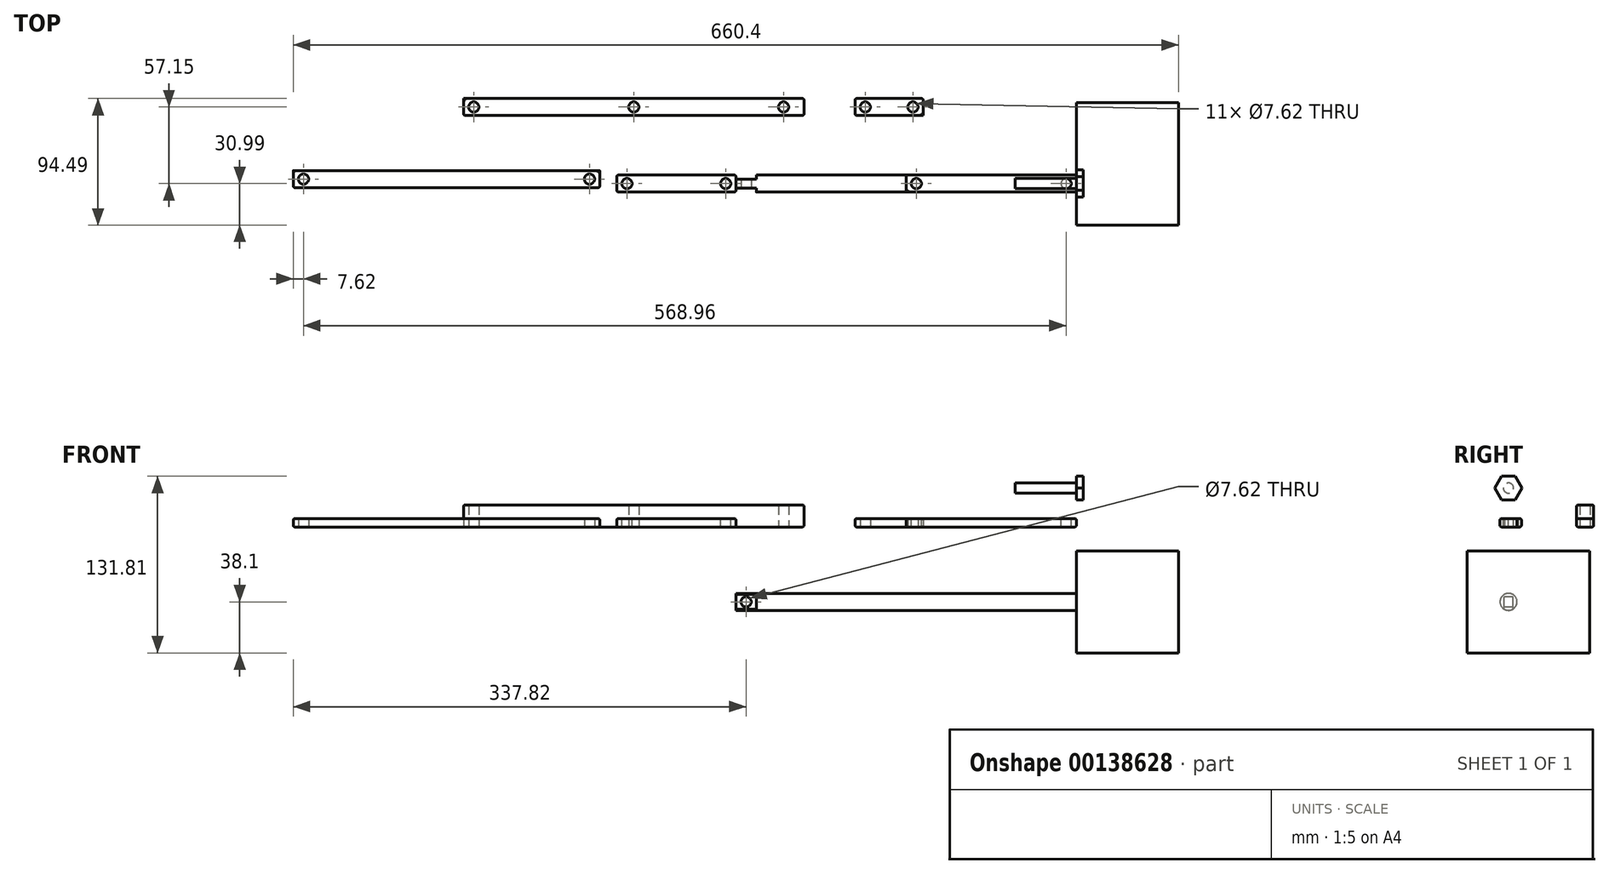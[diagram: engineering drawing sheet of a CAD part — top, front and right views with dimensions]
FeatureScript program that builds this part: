
annotation { "Feature Type Name" : "Feature", "Feature Type Description" : "" }
export const myFeature = defineFeature(function(context is Context, id is Id, definition is map)
    precondition{}
    {
        {
            var Q0;
            Q0=qCreatedBy(makeId("Right.planeOp"),FACE);
            var sketch = newSketch(context, id + "F0", { "sketchPlane" : qUnion([Q0])});
            skCircle(sketch, "E0", {"center": v(0, 0) * mm, "radius": 30.99 * mm});
            skSolve(sketch);
        }
        {
            var Q0;
            Q0 = qSketchRegion(id + "F0", true);
            extrude(context, id + "F1", {"entities" : qUnion([Q0]), "depth" : 76.2 * mm});
        }
        {
            var Q0;
            Q0=makeQuery(id+"F1.opExtrude","CAP_FACE",FACE,{"disambiguationData":[OSD([sQuery(id+"F0.wireOp",EDGE,"E0")])],"isStart":true});
            var sketch = newSketch(context, id + "F2", { "sketchPlane" : qUnion([Q0])});
            skCircle(sketch, "E1", {"center": v(0, 0) * mm, "radius": 6.35 * mm});
            skSolve(sketch);
        }
        {
            var Q0;
            Q0 = qSketchRegion(id + "F2", true);
            extrude(context, id + "F3", {"entities" : qUnion([Q0]), "operationType" : NewBodyOperationType.ADD, "depth" : 254 * mm});
        }
        {
            var Q0;
            Q0=qCreatedBy(makeId("Front.planeOp"),FACE);
            var sketch = newSketch(context, id + "F4", { "sketchPlane" : qUnion([Q0])});
            skCircle(sketch, "E2", {"center": v(-246.38, 0) * mm, "radius": 3.8 * mm});
            skSolve(sketch);
        }
        {
            var Q0;
            Q0 = qSketchRegion(id + "F4", true);
            extrude(context, id + "F5", {"entities" : qUnion([Q0]), "operationType" : NewBodyOperationType.REMOVE, "endBound" : BoundingType.SYMMETRIC, "oppositeDirection" : true, "depth" : 25.4 * mm});
        }
        {
            var Q0;
            Q0=qCreatedBy(makeId("Top.planeOp"),FACE);
            var sketch = newSketch(context, id + "F6", { "sketchPlane" : qUnion([Q0])});
            skLineSegment(sketch, "E3.bottom", {"start": v(-254, -6.35) * mm, "end": v(-238.76, -6.35) * mm});
            skLineSegment(sketch, "E3.top", {"start": v(-254, -3.3) * mm, "end": v(-238.76, -3.3) * mm});
            skLineSegment(sketch, "E3.left", {"start": v(-254, -6.35) * mm, "end": v(-254, -3.3) * mm});
            skLineSegment(sketch, "E3.right", {"start": v(-238.76, -6.35) * mm, "end": v(-238.76, -3.3) * mm});
            skLineSegment(sketch, "E4.bottom", {"start": v(-254, 6.35) * mm, "end": v(-238.76, 6.35) * mm});
            skLineSegment(sketch, "E4.top", {"start": v(-254, 3.3) * mm, "end": v(-238.76, 3.3) * mm});
            skLineSegment(sketch, "E4.left", {"start": v(-254, 6.35) * mm, "end": v(-254, 3.3) * mm});
            skLineSegment(sketch, "E4.right", {"start": v(-238.76, 6.35) * mm, "end": v(-238.76, 3.3) * mm});
            skSolve(sketch);
        }
        {
            var Q0;
            Q0 = qSketchRegion(id + "F6", true);
            extrude(context, id + "F7", {"entities" : qUnion([Q0]), "operationType" : NewBodyOperationType.REMOVE, "endBound" : BoundingType.SYMMETRIC, "oppositeDirection" : true, "depth" : 25.4 * mm});
        }
        {
            var Q0;
            Q0=qCreatedBy(makeId("Front.planeOp"),FACE);
            var sketch = newSketch(context, id + "F8", { "sketchPlane" : qUnion([Q0])});
            skLineSegment(sketch, "E5.bottom", {"start": v(0, 55.88) * mm, "end": v(-127, 55.88) * mm});
            skLineSegment(sketch, "E5.top", {"start": v(0, 62.23) * mm, "end": v(-127, 62.23) * mm});
            skLineSegment(sketch, "E5.left", {"start": v(0, 55.88) * mm, "end": v(0, 62.23) * mm});
            skLineSegment(sketch, "E5.right", {"start": v(-127, 55.88) * mm, "end": v(-127, 62.23) * mm});
            skSolve(sketch);
        }
        {
            var Q0;
            Q0=qCreatedBy(makeId("Top.planeOp"),FACE);
            cPlane(context, id + "F9", {"entities" : qUnion([Q0]), "cplaneType" : CPlaneType.OFFSET, "offset" : 55.88 * mm, "width" : 152.4 * mm, "height" : 152.4 * mm});
        }
        {
            var Q0;
            Q0=qCreatedBy(makeId("Top.planeOp"),FACE);
            var sketch = newSketch(context, id + "F10", { "sketchPlane" : qUnion([Q0])});
            skLineSegment(sketch, "E6.bottom", {"start": v(-238.76, 3.3) * mm, "end": v(-137.16, 3.3) * mm});
            skLineSegment(sketch, "E6.top", {"start": v(-238.76, 6.35) * mm, "end": v(-137.16, 6.35) * mm});
            skLineSegment(sketch, "E6.left", {"start": v(-238.76, 3.3) * mm, "end": v(-238.76, 6.35) * mm});
            skLineSegment(sketch, "E6.right", {"start": v(-137.16, 3.3) * mm, "end": v(-137.16, 6.35) * mm});
            skSolve(sketch);
        }
        {
            var Q0;
            Q0=qCreatedBy(makeId("Right.planeOp"),FACE);
            var sketch = newSketch(context, id + "F11", { "sketchPlane" : qUnion([Q0])});
            skCircle(sketch, "E7.cCircle", {"center": v(0, 84.9) * mm, "radius": 8.8 * mm, "construction": true});
            skLineSegment(sketch, "E7.0", {"start": v(5.08, 76.11) * mm, "end": v(-5.08, 76.11) * mm});
            skLineSegment(sketch, "E7.1", {"start": v(-5.08, 76.11) * mm, "end": v(-10.16, 84.9) * mm});
            skLineSegment(sketch, "E7.2", {"start": v(-10.16, 84.9) * mm, "end": v(-5.08, 93.7) * mm});
            skLineSegment(sketch, "E7.3", {"start": v(-5.08, 93.7) * mm, "end": v(5.08, 93.7) * mm});
            skLineSegment(sketch, "E7.4", {"start": v(5.08, 93.7) * mm, "end": v(10.16, 84.9) * mm});
            skLineSegment(sketch, "E7.5", {"start": v(10.16, 84.9) * mm, "end": v(5.08, 76.11) * mm});
            skPoint(sketch, "E7.0.midPoint", {"position": v(0, 76.11) * mm});
            skSolve(sketch);
        }
        {
            var Q0;
            Q0 = qSketchRegion(id + "F11", true);
            extrude(context, id + "F12", {"entities" : qUnion([Q0]), "depth" : 5.08 * mm});
        }
        {
            var Q0;
            Q0=makeQuery(id+"F12.opExtrude","CAP_FACE",FACE,{"disambiguationData":[OSD([sQuery(id+"F11.wireOp",EDGE,"E7.0"),sQuery(id+"F11.wireOp",EDGE,"E7.1"),sQuery(id+"F11.wireOp",EDGE,"E7.2"),sQuery(id+"F11.wireOp",EDGE,"E7.3"),sQuery(id+"F11.wireOp",EDGE,"E7.4"),sQuery(id+"F11.wireOp",EDGE,"E7.5")])],"isStart":false});
            var sketch = newSketch(context, id + "F13", { "sketchPlane" : qUnion([Q0])});
            skCircle(sketch, "E8", {"center": v(0, 84.9) * mm, "radius": 3.81 * mm});
            skSolve(sketch);
        }
        {
            var Q0;
            Q0 = qSketchRegion(id + "F13", true);
            extrude(context, id + "F14", {"entities" : qUnion([Q0]), "operationType" : NewBodyOperationType.ADD, "oppositeDirection" : true, "depth" : 50.8 * mm});
        }
        {
            var Q0;
            Q0=makeQuery(id+"F8.imprint","IMPRINT",FACE,{"disambiguationData":[TD([[makeQuery(id+"F8.imprint","IMPRINT",EDGE,{"derivedFrom":sQuery(id+"F8.wireOp",EDGE,"E5.bottom")}),-1.0]])]});
            extrude(context, id + "F15", {"entities" : qUnion([Q0]), "endBound" : BoundingType.SYMMETRIC, "depth" : 12.7 * mm});
        }
        {
            var Q0;
            Q0=makeQuery(id+"F15.opExtrude","SWEPT_FACE",FACE,{"disambiguationData":[OSD([sQuery(id+"F8.wireOp",EDGE,"E5.top")])]});
            var sketch = newSketch(context, id + "F16", { "sketchPlane" : qUnion([Q0])});
            skCircle(sketch, "E9", {"center": v(-7.62, 0) * mm, "radius": 3.81 * mm});
            skCircle(sketch, "E10", {"center": v(-119.38, 0) * mm, "radius": 3.81 * mm});
            skSolve(sketch);
        }
        {
            var Q0;
            Q0=makeQuery(id+"F16.imprint","IMPRINT",FACE,{"disambiguationData":[TD([[makeQuery(id+"F16.imprint","IMPRINT",EDGE,{"derivedFrom":sQuery(id+"F16.wireOp",EDGE,"E10")}),1.0]])]});
            var Q1;
            Q1=makeQuery(id+"F16.imprint","IMPRINT",FACE,{"disambiguationData":[TD([[makeQuery(id+"F16.imprint","IMPRINT",EDGE,{"derivedFrom":sQuery(id+"F16.wireOp",EDGE,"E9")}),1.0]])]});
            extrude(context, id + "F17", {"entities" : qUnion([Q0, Q1]), "operationType" : NewBodyOperationType.REMOVE, "oppositeDirection" : true, "depth" : 12.7 * mm});
        }
        {
            var Q0;
            Q0=qCreatedBy(id+"F9.planeOp",FACE);
            var sketch = newSketch(context, id + "F18", { "sketchPlane" : qUnion([Q0])});
            skLineSegment(sketch, "E11.bottom", {"start": v(-254, 6.35) * mm, "end": v(-342.9, 6.35) * mm});
            skLineSegment(sketch, "E11.top", {"start": v(-254, -6.35) * mm, "end": v(-342.9, -6.35) * mm});
            skLineSegment(sketch, "E11.left", {"start": v(-254, 6.35) * mm, "end": v(-254, -6.35) * mm});
            skLineSegment(sketch, "E11.right", {"start": v(-342.9, 6.35) * mm, "end": v(-342.9, -6.35) * mm});
            skSolve(sketch);
        }
        {
            var Q0;
            Q0 = qSketchRegion(id + "F18", true);
            extrude(context, id + "F19", {"entities" : qUnion([Q0]), "depth" : 6.35 * mm});
        }
        {
            var Q0;
            Q0=makeQuery(id+"F19.opExtrude","CAP_FACE",FACE,{"disambiguationData":[OSD([sQuery(id+"F18.wireOp",EDGE,"E11.bottom"),sQuery(id+"F18.wireOp",EDGE,"E11.top"),sQuery(id+"F18.wireOp",EDGE,"E11.left"),sQuery(id+"F18.wireOp",EDGE,"E11.right")])],"isStart":false});
            var sketch = newSketch(context, id + "F20", { "sketchPlane" : qUnion([Q0])});
            skCircle(sketch, "E12", {"center": v(-261.62, 0) * mm, "radius": 3.81 * mm});
            skPoint(sketch, "E12.centerSnap0", {"position": v(-254, 0) * mm});
            skCircle(sketch, "E13", {"center": v(-335.28, 0) * mm, "radius": 3.81 * mm});
            skSolve(sketch);
        }
        {
            var Q0;
            Q0 = qSketchRegion(id + "F20", true);
            extrude(context, id + "F21", {"entities" : qUnion([Q0]), "operationType" : NewBodyOperationType.REMOVE, "endBound" : BoundingType.SYMMETRIC, "oppositeDirection" : true, "depth" : 12.7 * mm});
        }
        {
            var Q0;
            Q0=qCreatedBy(id+"F9.planeOp",FACE);
            var sketch = newSketch(context, id + "F22", { "sketchPlane" : qUnion([Q0])});
            skLineSegment(sketch, "E14.bottom", {"start": v(-355.6, 9.65) * mm, "end": v(-584.2, 9.65) * mm});
            skLineSegment(sketch, "E14.top", {"start": v(-355.6, -3.05) * mm, "end": v(-584.2, -3.05) * mm});
            skLineSegment(sketch, "E14.left", {"start": v(-355.6, 9.65) * mm, "end": v(-355.6, -3.05) * mm});
            skLineSegment(sketch, "E14.right", {"start": v(-584.2, 9.65) * mm, "end": v(-584.2, -3.05) * mm});
            skCircle(sketch, "E15", {"center": v(-576.58, 3.3) * mm, "radius": 3.81 * mm});
            skCircle(sketch, "E16", {"center": v(-363.22, 3.3) * mm, "radius": 3.81 * mm});
            skSolve(sketch);
        }
        {
            var Q0;
            Q0 = qSketchRegion(id + "F22", true);
            extrude(context, id + "F23", {"entities" : qUnion([Q0]), "depth" : 6.35 * mm});
        }
        {
            var Q0;
            Q0=qCreatedBy(id+"F9.planeOp",FACE);
            var sketch = newSketch(context, id + "F24", { "sketchPlane" : qUnion([Q0])});
            skLineSegment(sketch, "E17.bottom", {"start": v(-203.2, 63.5) * mm, "end": v(-457.2, 63.5) * mm});
            skLineSegment(sketch, "E17.top", {"start": v(-203.2, 50.8) * mm, "end": v(-457.2, 50.8) * mm});
            skLineSegment(sketch, "E17.left", {"start": v(-203.2, 63.5) * mm, "end": v(-203.2, 50.8) * mm});
            skLineSegment(sketch, "E17.right", {"start": v(-457.2, 63.5) * mm, "end": v(-457.2, 50.8) * mm});
            skCircle(sketch, "E18", {"center": v(-449.58, 57.15) * mm, "radius": 3.81 * mm});
            skCircle(sketch, "E19", {"center": v(-218.44, 57.15) * mm, "radius": 3.81 * mm});
            skCircle(sketch, "E20", {"center": v(-330.2, 57.15) * mm, "radius": 3.81 * mm});
            skSolve(sketch);
        }
        {
            var Q0;
            Q0 = qSketchRegion(id + "F24", true);
            extrude(context, id + "F25", {"entities" : qUnion([Q0]), "depth" : 16.5 * mm});
        }
        {
            var Q0;
            Q0=qCreatedBy(id+"F9.planeOp",FACE);
            var sketch = newSketch(context, id + "F26", { "sketchPlane" : qUnion([Q0])});
            skLineSegment(sketch, "E21.bottom", {"start": v(-165.1, 50.8) * mm, "end": v(-114.3, 50.8) * mm});
            skLineSegment(sketch, "E21.top", {"start": v(-165.1, 63.5) * mm, "end": v(-114.3, 63.5) * mm});
            skLineSegment(sketch, "E21.left", {"start": v(-165.1, 50.8) * mm, "end": v(-165.1, 63.5) * mm});
            skLineSegment(sketch, "E21.right", {"start": v(-114.3, 50.8) * mm, "end": v(-114.3, 63.5) * mm});
            skCircle(sketch, "E22", {"center": v(-157.48, 57.15) * mm, "radius": 3.81 * mm});
            skCircle(sketch, "E23", {"center": v(-121.92, 57.15) * mm, "radius": 3.81 * mm});
            skSolve(sketch);
        }
        {
            var Q0;
            Q0 = qSketchRegion(id + "F26", true);
            extrude(context, id + "F27", {"entities" : qUnion([Q0]), "depth" : 6.35 * mm});
        }
        {
            var Q0;
            Q0=makeQuery(id+"F27.opExtrude","CAP_EDGE",EDGE,{"disambiguationData":[OSD([sQuery(id+"F26.wireOp",EDGE,"E21.bottom")])],"isStart":false});
            var Q1;
            Q1=makeQuery(id+"F27.opExtrude","CAP_EDGE",EDGE,{"disambiguationData":[OSD([sQuery(id+"F26.wireOp",EDGE,"E21.left")])],"isStart":false});
            var Q2;
            Q2=makeQuery(id+"F27.opExtrude","CAP_EDGE",EDGE,{"disambiguationData":[OSD([sQuery(id+"F26.wireOp",EDGE,"E21.top")])],"isStart":false});
            var Q3;
            Q3=makeQuery(id+"F27.opExtrude","CAP_EDGE",EDGE,{"disambiguationData":[OSD([sQuery(id+"F26.wireOp",EDGE,"E21.right")])],"isStart":false});
            var Q4;
            Q4=makeQuery(id+"F27.opExtrude","SWEPT_EDGE",EDGE,{"disambiguationData":[OSD([sQuery(id+"F26.wireOp",EDGE,"E21.bottom"),sQuery(id+"F26.wireOp",EDGE,"E21.left")])]});
            var Q5;
            Q5=makeQuery(id+"F27.opExtrude","CAP_EDGE",EDGE,{"disambiguationData":[OSD([sQuery(id+"F26.wireOp",EDGE,"E21.bottom")])],"isStart":true});
            var Q6;
            Q6=makeQuery(id+"F27.opExtrude","CAP_EDGE",EDGE,{"disambiguationData":[OSD([sQuery(id+"F26.wireOp",EDGE,"E21.left")])],"isStart":true});
            var Q7;
            Q7=makeQuery(id+"F27.opExtrude","CAP_EDGE",EDGE,{"disambiguationData":[OSD([sQuery(id+"F26.wireOp",EDGE,"E21.right")])],"isStart":true});
            var Q8;
            Q8=makeQuery(id+"F27.opExtrude","SWEPT_EDGE",EDGE,{"disambiguationData":[OSD([sQuery(id+"F26.wireOp",EDGE,"E21.top"),sQuery(id+"F26.wireOp",EDGE,"E21.right")])]});
            var Q9;
            Q9=makeQuery(id+"F27.opExtrude","CAP_EDGE",EDGE,{"disambiguationData":[OSD([sQuery(id+"F26.wireOp",EDGE,"E21.top")])],"isStart":true});
            var Q10;
            Q10=makeQuery(id+"F27.opExtrude","SWEPT_EDGE",EDGE,{"disambiguationData":[OSD([sQuery(id+"F26.wireOp",EDGE,"E21.top"),sQuery(id+"F26.wireOp",EDGE,"E21.left")])]});
            fillet(context, id + "F28", {"entities" : qUnion([Q0, Q1, Q2, Q3, Q4, Q5, Q6, Q7, Q8, Q9, Q10]), "radius" : 1.27 * mm, "tangentPropagation" : true, "allowEdgeOverflow" : false});
        }
        {
            var Q0;
            Q0=makeQuery(id+"F15.opExtrude","CAP_EDGE",EDGE,{"disambiguationData":[OSD([sQuery(id+"F8.wireOp",EDGE,"E5.top")])],"isStart":true});
            var Q1;
            Q1=makeQuery(id+"F15.opExtrude","CAP_EDGE",EDGE,{"disambiguationData":[OSD([sQuery(id+"F8.wireOp",EDGE,"E5.top")])],"isStart":false});
            var Q2;
            Q2=makeQuery(id+"F15.opExtrude","SWEPT_EDGE",EDGE,{"disambiguationData":[OSD([sQuery(id+"F8.wireOp",EDGE,"E5.top"),sQuery(id+"F8.wireOp",EDGE,"E5.left")])]});
            var Q3;
            Q3=makeQuery(id+"F15.opExtrude","SWEPT_EDGE",EDGE,{"disambiguationData":[OSD([sQuery(id+"F8.wireOp",EDGE,"E5.top"),sQuery(id+"F8.wireOp",EDGE,"E5.right")])]});
            var Q4;
            Q4=makeQuery(id+"F15.opExtrude","CAP_EDGE",EDGE,{"disambiguationData":[OSD([sQuery(id+"F8.wireOp",EDGE,"E5.bottom")])],"isStart":false});
            var Q5;
            Q5=makeQuery(id+"F15.opExtrude","CAP_EDGE",EDGE,{"disambiguationData":[OSD([sQuery(id+"F8.wireOp",EDGE,"E5.bottom")])],"isStart":true});
            var Q6;
            Q6=makeQuery(id+"F15.opExtrude","SWEPT_EDGE",EDGE,{"disambiguationData":[OSD([sQuery(id+"F8.wireOp",EDGE,"E5.bottom"),sQuery(id+"F8.wireOp",EDGE,"E5.right")])]});
            var Q7;
            Q7=makeQuery(id+"F15.opExtrude","CAP_EDGE",EDGE,{"disambiguationData":[OSD([sQuery(id+"F8.wireOp",EDGE,"E5.left")])],"isStart":true});
            var Q8;
            Q8=makeQuery(id+"F15.opExtrude","SWEPT_EDGE",EDGE,{"disambiguationData":[OSD([sQuery(id+"F8.wireOp",EDGE,"E5.bottom"),sQuery(id+"F8.wireOp",EDGE,"E5.left")])]});
            var Q9;
            Q9=makeQuery(id+"F15.opExtrude","CAP_FACE",FACE,{"disambiguationData":[OSD([sQuery(id+"F8.wireOp",EDGE,"E5.bottom"),sQuery(id+"F8.wireOp",EDGE,"E5.top"),sQuery(id+"F8.wireOp",EDGE,"E5.left"),sQuery(id+"F8.wireOp",EDGE,"E5.right")])],"isStart":true});
            var Q10;
            Q10=makeQuery(id+"F15.opExtrude","CAP_EDGE",EDGE,{"disambiguationData":[OSD([sQuery(id+"F8.wireOp",EDGE,"E5.left")])],"isStart":false});
            fillet(context, id + "F29", {"entities" : qUnion([Q0, Q1, Q2, Q3, Q4, Q5, Q6, Q7, Q8, Q9, Q10]), "radius" : 1.27 * mm, "tangentPropagation" : true, "allowEdgeOverflow" : false});
        }
        {
            var Q0;
            Q0=makeQuery(id+"F25.opExtrude","CAP_EDGE",EDGE,{"disambiguationData":[OSD([sQuery(id+"F24.wireOp",EDGE,"E17.bottom")])],"isStart":false});
            var Q1;
            Q1=makeQuery(id+"F25.opExtrude","CAP_EDGE",EDGE,{"disambiguationData":[OSD([sQuery(id+"F24.wireOp",EDGE,"E17.bottom")])],"isStart":true});
            var Q2;
            Q2=makeQuery(id+"F19.opExtrude","CAP_EDGE",EDGE,{"disambiguationData":[OSD([sQuery(id+"F18.wireOp",EDGE,"E11.bottom")])],"isStart":false});
            var Q3;
            Q3=makeQuery(id+"F19.opExtrude","CAP_EDGE",EDGE,{"disambiguationData":[OSD([sQuery(id+"F18.wireOp",EDGE,"E11.bottom")])],"isStart":true});
            var Q4;
            Q4=makeQuery(id+"F25.opExtrude","CAP_EDGE",EDGE,{"disambiguationData":[OSD([sQuery(id+"F24.wireOp",EDGE,"E17.right")])],"isStart":false});
            var Q5;
            Q5=makeQuery(id+"F25.opExtrude","CAP_EDGE",EDGE,{"disambiguationData":[OSD([sQuery(id+"F24.wireOp",EDGE,"E17.top")])],"isStart":false});
            var Q6;
            Q6=makeQuery(id+"F25.opExtrude","CAP_EDGE",EDGE,{"disambiguationData":[OSD([sQuery(id+"F24.wireOp",EDGE,"E17.left")])],"isStart":false});
            var Q7;
            Q7=makeQuery(id+"F25.opExtrude","SWEPT_EDGE",EDGE,{"disambiguationData":[OSD([sQuery(id+"F24.wireOp",EDGE,"E17.top"),sQuery(id+"F24.wireOp",EDGE,"E17.left")])]});
            var Q8;
            Q8=makeQuery(id+"F25.opExtrude","CAP_EDGE",EDGE,{"disambiguationData":[OSD([sQuery(id+"F24.wireOp",EDGE,"E17.left")])],"isStart":true});
            var Q9;
            Q9=makeQuery(id+"F25.opExtrude","SWEPT_EDGE",EDGE,{"disambiguationData":[OSD([sQuery(id+"F24.wireOp",EDGE,"E17.bottom"),sQuery(id+"F24.wireOp",EDGE,"E17.left")])]});
            var Q10;
            Q10=makeQuery(id+"F25.opExtrude","SWEPT_EDGE",EDGE,{"disambiguationData":[OSD([sQuery(id+"F24.wireOp",EDGE,"E17.top"),sQuery(id+"F24.wireOp",EDGE,"E17.right")])]});
            var Q11;
            Q11=makeQuery(id+"F25.opExtrude","CAP_EDGE",EDGE,{"disambiguationData":[OSD([sQuery(id+"F24.wireOp",EDGE,"E17.right")])],"isStart":true});
            var Q12;
            Q12=makeQuery(id+"F25.opExtrude","CAP_EDGE",EDGE,{"disambiguationData":[OSD([sQuery(id+"F24.wireOp",EDGE,"E17.top")])],"isStart":true});
            var Q13;
            Q13=makeQuery(id+"F23.opExtrude","CAP_EDGE",EDGE,{"disambiguationData":[OSD([sQuery(id+"F22.wireOp",EDGE,"E14.top")])],"isStart":false});
            var Q14;
            Q14=makeQuery(id+"F23.opExtrude","CAP_EDGE",EDGE,{"disambiguationData":[OSD([sQuery(id+"F22.wireOp",EDGE,"E14.top")])],"isStart":true});
            var Q15;
            Q15=makeQuery(id+"F23.opExtrude","CAP_EDGE",EDGE,{"disambiguationData":[OSD([sQuery(id+"F22.wireOp",EDGE,"E14.bottom")])],"isStart":false});
            var Q16;
            Q16=makeQuery(id+"F23.opExtrude","CAP_EDGE",EDGE,{"disambiguationData":[OSD([sQuery(id+"F22.wireOp",EDGE,"E14.bottom")])],"isStart":true});
            var Q17;
            Q17=makeQuery(id+"F23.opExtrude","CAP_EDGE",EDGE,{"disambiguationData":[OSD([sQuery(id+"F22.wireOp",EDGE,"E14.right")])],"isStart":false});
            var Q18;
            Q18=makeQuery(id+"F23.opExtrude","CAP_EDGE",EDGE,{"disambiguationData":[OSD([sQuery(id+"F22.wireOp",EDGE,"E14.right")])],"isStart":true});
            var Q19;
            Q19=makeQuery(id+"F23.opExtrude","CAP_EDGE",EDGE,{"disambiguationData":[OSD([sQuery(id+"F22.wireOp",EDGE,"E14.left")])],"isStart":false});
            var Q20;
            Q20=makeQuery(id+"F23.opExtrude","CAP_EDGE",EDGE,{"disambiguationData":[OSD([sQuery(id+"F22.wireOp",EDGE,"E14.left")])],"isStart":true});
            var Q21;
            Q21=makeQuery(id+"F23.opExtrude","SWEPT_EDGE",EDGE,{"disambiguationData":[OSD([sQuery(id+"F22.wireOp",EDGE,"E14.top"),sQuery(id+"F22.wireOp",EDGE,"E14.left")])]});
            var Q22;
            Q22=makeQuery(id+"F23.opExtrude","SWEPT_EDGE",EDGE,{"disambiguationData":[OSD([sQuery(id+"F22.wireOp",EDGE,"E14.top"),sQuery(id+"F22.wireOp",EDGE,"E14.right")])]});
            var Q23;
            Q23=makeQuery(id+"F19.opExtrude","CAP_EDGE",EDGE,{"disambiguationData":[OSD([sQuery(id+"F18.wireOp",EDGE,"E11.right")])],"isStart":false});
            var Q24;
            Q24=makeQuery(id+"F19.opExtrude","CAP_EDGE",EDGE,{"disambiguationData":[OSD([sQuery(id+"F18.wireOp",EDGE,"E11.top")])],"isStart":false});
            var Q25;
            Q25=makeQuery(id+"F19.opExtrude","CAP_EDGE",EDGE,{"disambiguationData":[OSD([sQuery(id+"F18.wireOp",EDGE,"E11.left")])],"isStart":true});
            var Q26;
            Q26=makeQuery(id+"F19.opExtrude","SWEPT_EDGE",EDGE,{"disambiguationData":[OSD([sQuery(id+"F18.wireOp",EDGE,"E11.top"),sQuery(id+"F18.wireOp",EDGE,"E11.left")])]});
            var Q27;
            Q27=makeQuery(id+"F19.opExtrude","SWEPT_EDGE",EDGE,{"disambiguationData":[OSD([sQuery(id+"F18.wireOp",EDGE,"E11.bottom"),sQuery(id+"F18.wireOp",EDGE,"E11.left")])]});
            var Q28;
            Q28=makeQuery(id+"F19.opExtrude","CAP_EDGE",EDGE,{"disambiguationData":[OSD([sQuery(id+"F18.wireOp",EDGE,"E11.left")])],"isStart":false});
            var Q29;
            Q29=makeQuery(id+"F19.opExtrude","SWEPT_EDGE",EDGE,{"disambiguationData":[OSD([sQuery(id+"F18.wireOp",EDGE,"E11.bottom"),sQuery(id+"F18.wireOp",EDGE,"E11.right")])]});
            var Q30;
            Q30=makeQuery(id+"F19.opExtrude","SWEPT_EDGE",EDGE,{"disambiguationData":[OSD([sQuery(id+"F18.wireOp",EDGE,"E11.top"),sQuery(id+"F18.wireOp",EDGE,"E11.right")])]});
            var Q31;
            Q31=makeQuery(id+"F19.opExtrude","CAP_EDGE",EDGE,{"disambiguationData":[OSD([sQuery(id+"F18.wireOp",EDGE,"E11.right")])],"isStart":true});
            var Q32;
            Q32=makeQuery(id+"F19.opExtrude","CAP_EDGE",EDGE,{"disambiguationData":[OSD([sQuery(id+"F18.wireOp",EDGE,"E11.top")])],"isStart":true});
            fillet(context, id + "F30", {"entities" : qUnion([Q0, Q1, Q2, Q3, Q4, Q5, Q6, Q7, Q8, Q9, Q10, Q11, Q12, Q13, Q14, Q15, Q16, Q17, Q18, Q19, Q20, Q21, Q22, Q23, Q24, Q25, Q26, Q27, Q28, Q29, Q30, Q31, Q32]), "radius" : 1.27 * mm, "tangentPropagation" : true, "allowEdgeOverflow" : false});
        }
        {
            var Q0;
            Q0=qCreatedBy(makeId("Right.planeOp"),FACE);
            var sketch = newSketch(context, id + "F31", { "sketchPlane" : qUnion([Q0])});
            skCircle(sketch, "E24.0", {"center": v(0, 0) * mm, "radius": 30.99 * mm});
            skLineSegment(sketch, "E25.bottom", {"start": v(-30.99, 38.1) * mm, "end": v(60.45, 38.1) * mm});
            skLineSegment(sketch, "E25.top", {"start": v(-30.99, -38.1) * mm, "end": v(60.45, -38.1) * mm});
            skLineSegment(sketch, "E25.left", {"start": v(-30.99, 38.1) * mm, "end": v(-30.99, -38.1) * mm});
            skLineSegment(sketch, "E25.right", {"start": v(60.45, 38.1) * mm, "end": v(60.45, -38.1) * mm});
            skSolve(sketch);
        }
        {
            var Q0;
            Q0 = qSketchRegion(id + "F31", true);
            extrude(context, id + "F32", {"entities" : qUnion([Q0]), "operationType" : NewBodyOperationType.ADD, "depth" : 76.2 * mm});
        }
    });
